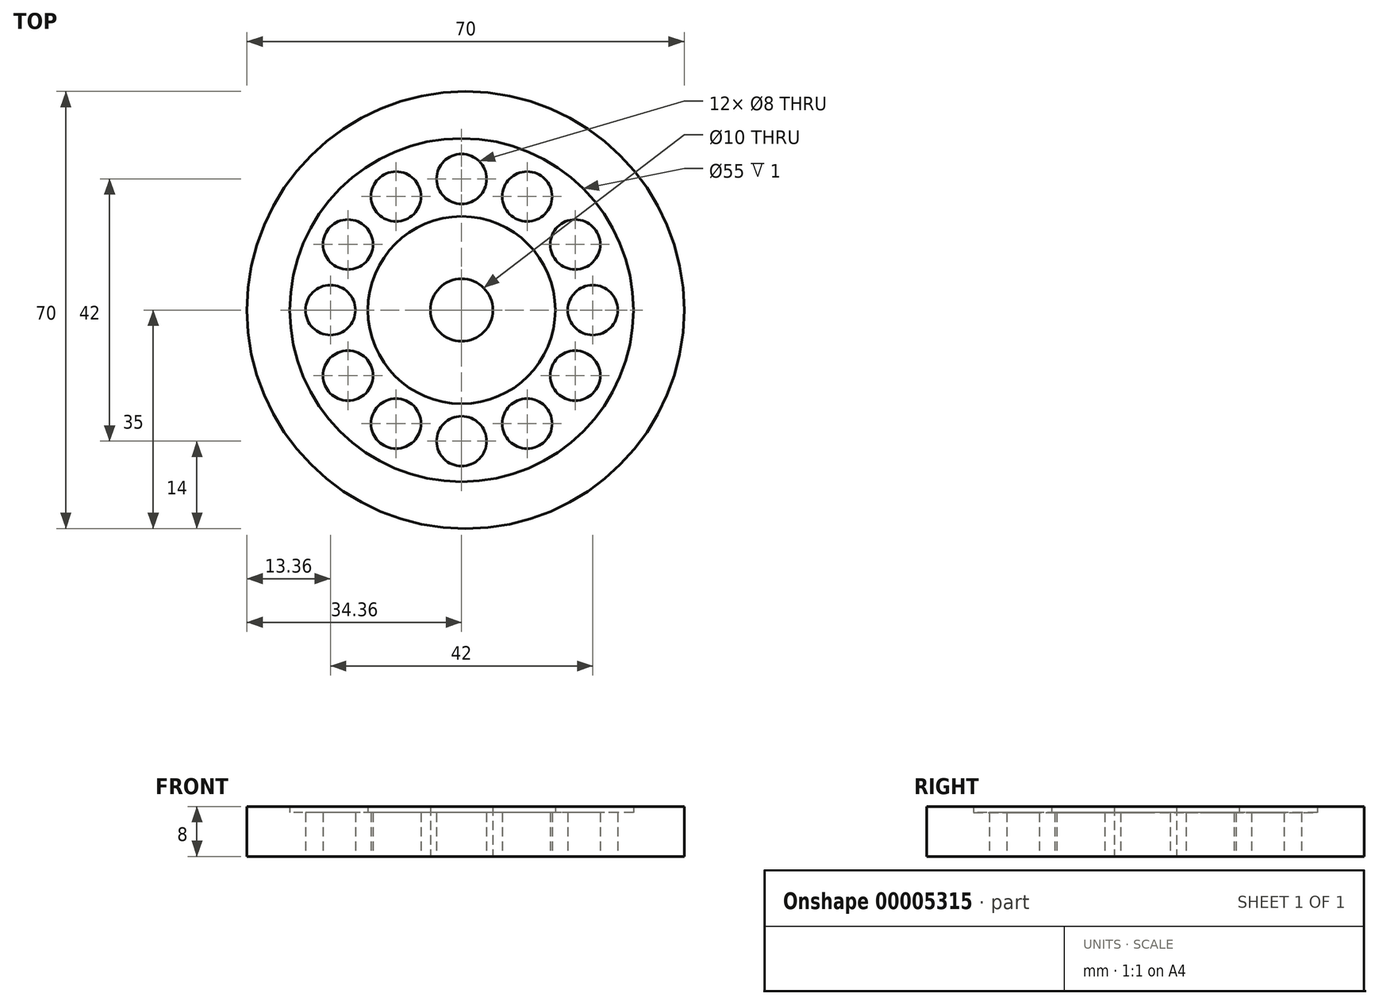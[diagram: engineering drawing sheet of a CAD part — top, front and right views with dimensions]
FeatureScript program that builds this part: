
annotation { "Feature Type Name" : "Feature", "Feature Type Description" : "" }
export const myFeature = defineFeature(function(context is Context, id is Id, definition is map)
    precondition{}
    {
        {
            var Q0;
            Q0=qCreatedBy(makeId("Top.planeOp"),FACE);
            var sketch = newSketch(context, id + "F0", { "sketchPlane" : qUnion([Q0])});
            skCircle(sketch, "E0", {"center": v(0, 0) * mm, "radius": 5 * mm});
            skCircle(sketch, "E1", {"center": v(0, 0) * mm, "radius": 21 * mm});
            skCircle(sketch, "E2", {"center": v(0, 0) * mm, "radius": 27.5 * mm});
            skCircle(sketch, "E3", {"center": v(0, 0) * mm, "radius": 15 * mm});
            skCircle(sketch, "E4", {"center": v(0.64, 0) * mm, "radius": 35 * mm});
            skCircle(sketch, "E5", {"center": v(0, 21) * mm, "radius": 4 * mm});
            skCircle(sketch, "E6.1.0", {"center": v(-10.5, 18.19) * mm, "radius": 4 * mm});
            skCircle(sketch, "E6.2.0", {"center": v(-18.19, 10.5) * mm, "radius": 4 * mm});
            skCircle(sketch, "E6.3.0", {"center": v(-21, 0) * mm, "radius": 4 * mm});
            skCircle(sketch, "E6.4.0", {"center": v(-18.19, -10.5) * mm, "radius": 4 * mm});
            skCircle(sketch, "E6.5.0", {"center": v(-10.5, -18.19) * mm, "radius": 4 * mm});
            skCircle(sketch, "E6.6.0", {"center": v(0, -21) * mm, "radius": 4 * mm});
            skCircle(sketch, "E6.7.0", {"center": v(10.5, -18.19) * mm, "radius": 4 * mm});
            skCircle(sketch, "E6.8.0", {"center": v(18.19, -10.5) * mm, "radius": 4 * mm});
            skCircle(sketch, "E6.9.0", {"center": v(21, 0) * mm, "radius": 4 * mm});
            skCircle(sketch, "E6.10.0", {"center": v(18.19, 10.5) * mm, "radius": 4 * mm});
            skCircle(sketch, "E6.11.0", {"center": v(10.5, 18.19) * mm, "radius": 4 * mm});
            skSolve(sketch);
        }
        {
            var Q0;
            Q0=makeQuery(id+"F0.imprint","IMPRINT",FACE,{"disambiguationData":[TD([[makeQuery(id+"F0.imprint","IMPRINT",EDGE,{"derivedFrom":sQuery(id+"F0.wireOp",EDGE,"E2")}),-1.0]])]});
            var Q1;
            Q1=makeQuery(id+"F0.imprint","IMPRINT",FACE,{"disambiguationData":[TD([[makeQuery(id+"F0.imprint","IMPRINT",EDGE,{"derivedFrom":sQuery(id+"F0.wireOp",EDGE,"E0")}),-1.0]])]});
            extrude(context, id + "F1", {"entities" : qUnion([Q0, Q1]), "depth" : 8 * mm});
        }
        {
            var Q0;
            Q0=makeQuery(id+"F0.imprint","IMPRINT",FACE,{"disambiguationData":[TD([[makeQuery(id+"F0.imprint","IMPRINT",EDGE,{"derivedFrom":sQuery(id+"F0.wireOp",EDGE,"E2")}),1.0]])]});
            var Q1;
            Q1=makeQuery(id+"F0.imprint","IMPRINT",FACE,{"disambiguationData":[TD([[makeQuery(id+"F0.imprint","IMPRINT",EDGE,{"derivedFrom":sQuery(id+"F0.wireOp",EDGE,"E3")}),-1.0]])]});
            extrude(context, id + "F2", {"entities" : qUnion([Q0, Q1]), "operationType" : NewBodyOperationType.ADD, "depth" : 7 * mm});
        }
    });
